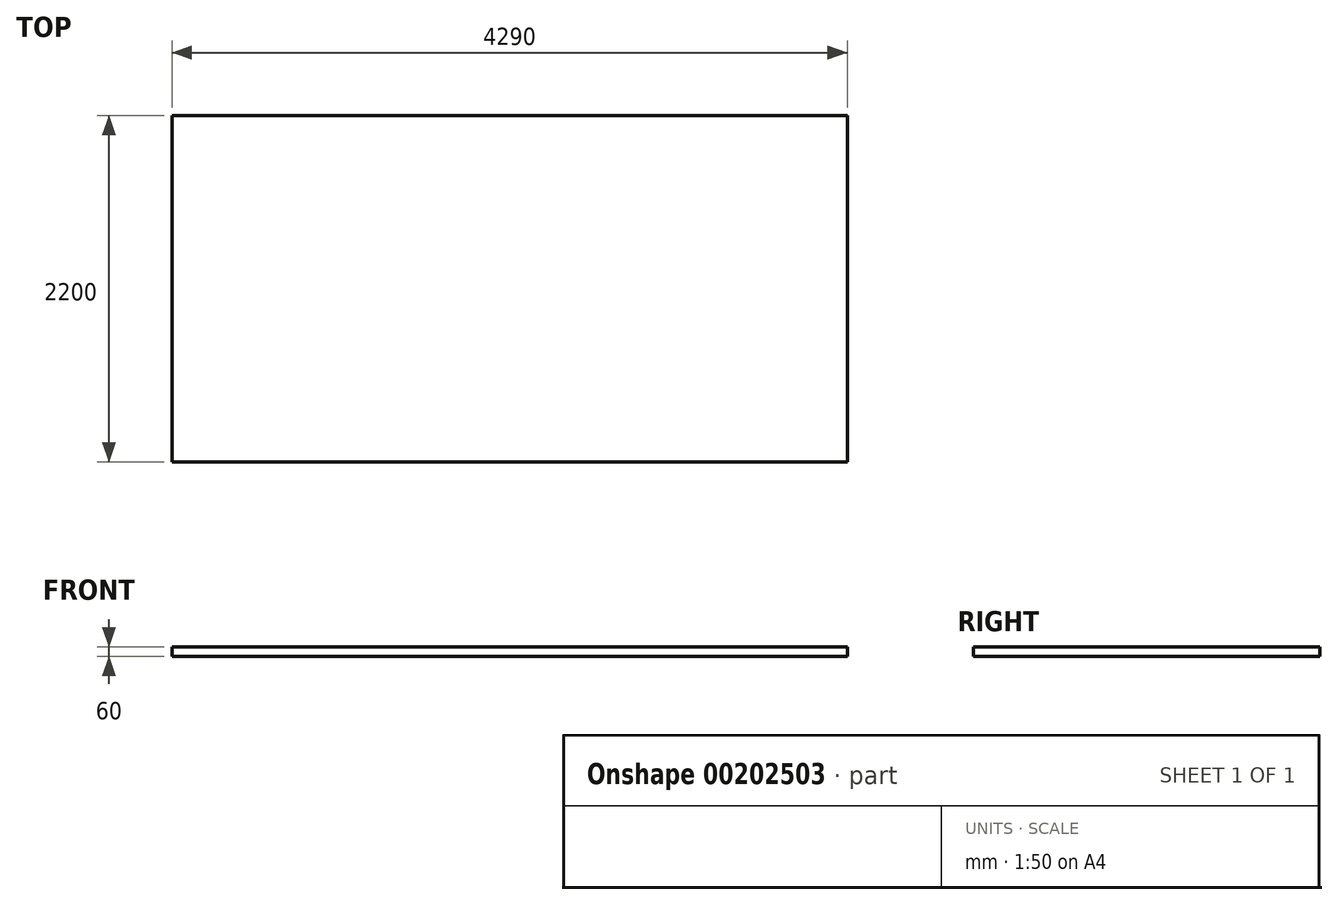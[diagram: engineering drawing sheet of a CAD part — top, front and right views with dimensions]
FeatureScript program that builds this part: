
annotation { "Feature Type Name" : "Feature", "Feature Type Description" : "" }
export const myFeature = defineFeature(function(context is Context, id is Id, definition is map)
    precondition{}
    {
        {
            var Q0;
            Q0=qCreatedBy(makeId("Top.planeOp"),FACE);
            var sketch = newSketch(context, id + "F0", { "sketchPlane" : qUnion([Q0])});
            skLineSegment(sketch, "E0.bottom", {"start": v(-2162.4, 1580.73) * mm, "end": v(2127.6, 1580.73) * mm});
            skLineSegment(sketch, "E0.top", {"start": v(-2162.4, -619.27) * mm, "end": v(2127.6, -619.27) * mm});
            skLineSegment(sketch, "E0.left", {"start": v(-2162.4, 1580.73) * mm, "end": v(-2162.4, -619.27) * mm});
            skLineSegment(sketch, "E0.right", {"start": v(2127.6, 1580.73) * mm, "end": v(2127.6, -619.27) * mm});
            skSolve(sketch);
        }
        {
            var Q0;
            Q0=makeQuery(id+"F0.imprint","IMPRINT",FACE,{"disambiguationData":[TD([[makeQuery(id+"F0.imprint","IMPRINT",EDGE,{"derivedFrom":sQuery(id+"F0.wireOp",EDGE,"E0.bottom")}),-1.0]])]});
            extrude(context, id + "F1", {"entities" : qUnion([Q0]), "depth" : 60 * mm});
        }
    });
